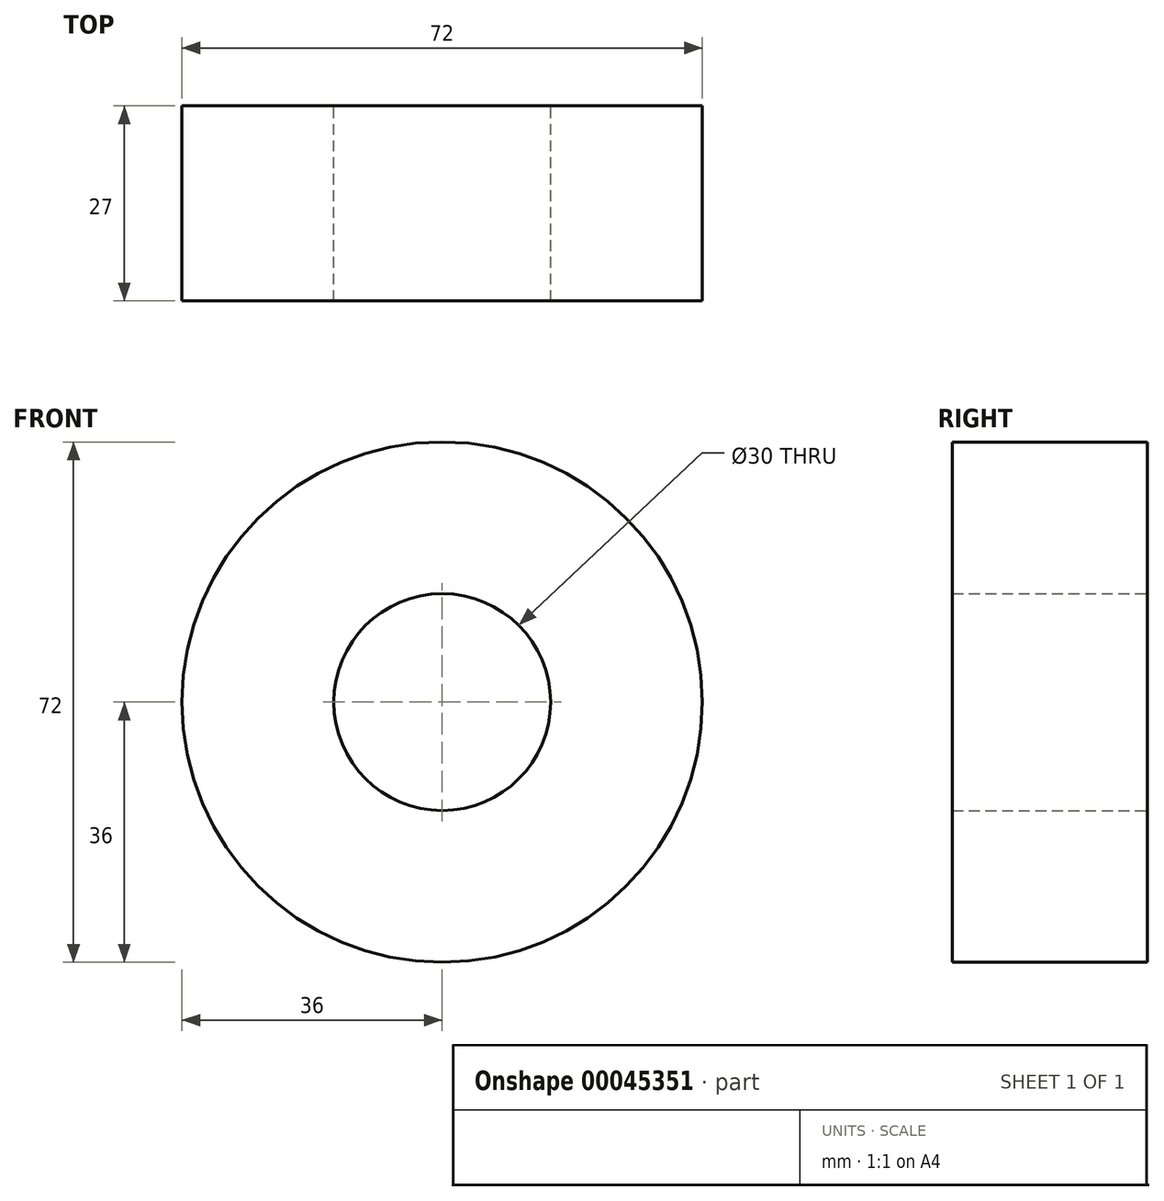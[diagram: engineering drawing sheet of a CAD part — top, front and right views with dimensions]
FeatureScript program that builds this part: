
annotation { "Feature Type Name" : "Feature", "Feature Type Description" : "" }
export const myFeature = defineFeature(function(context is Context, id is Id, definition is map)
    precondition{}
    {
        {
            var Q0;
            Q0=qCreatedBy(makeId("Front.planeOp"),FACE);
            var sketch = newSketch(context, id + "F0", { "sketchPlane" : qUnion([Q0])});
            skCircle(sketch, "E0", {"center": v(0, 0) * mm, "radius": 36 * mm});
            skCircle(sketch, "E1", {"center": v(0, 0) * mm, "radius": 15 * mm});
            skSolve(sketch);
        }
        {
            var Q0;
            Q0 = qSketchRegion(id + "F0", true);
            extrude(context, id + "F1", {"entities" : qUnion([Q0]), "depth" : 27 * mm});
        }
    });
